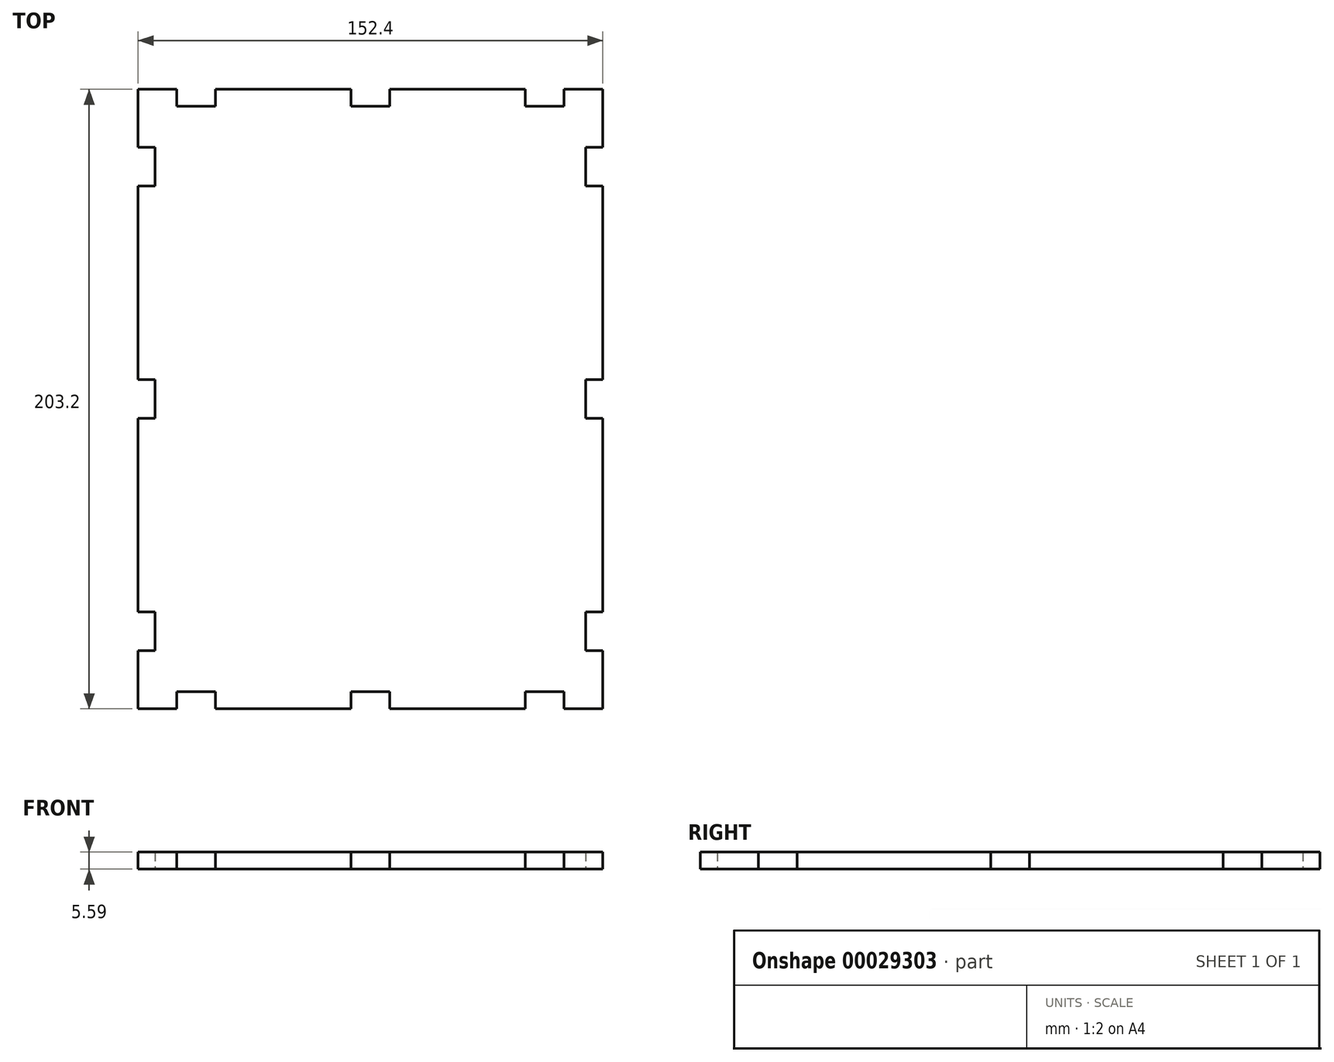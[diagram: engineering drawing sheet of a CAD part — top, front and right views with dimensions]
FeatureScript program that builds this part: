
annotation { "Feature Type Name" : "Feature", "Feature Type Description" : "" }
export const myFeature = defineFeature(function(context is Context, id is Id, definition is map)
    precondition{}
    {
        {
            var Q0;
            Q0=qCreatedBy(makeId("Top.planeOp"),FACE);
            var sketch = newSketch(context, id + "F0", { "sketchPlane" : qUnion([Q0])});
            skLineSegment(sketch, "E0", {"start": v(0, -101.6) * mm, "end": v(0, 101.6) * mm, "construction": true});
            skLineSegment(sketch, "E1", {"start": v(-76.2, 0) * mm, "end": v(76.2, 0) * mm, "construction": true});
            skLineSegment(sketch, "E2.0", {"start": v(38.1, -101.6) * mm, "end": v(38.1, 101.6) * mm, "construction": true});
            skLineSegment(sketch, "E3.0", {"start": v(76.2, -101.6) * mm, "end": v(76.2, -82.55) * mm, "construction": true});
            skLineSegment(sketch, "E4.0", {"start": v(-38.1, -101.6) * mm, "end": v(-38.1, 101.6) * mm, "construction": true});
            skLineSegment(sketch, "E5.0", {"start": v(-76.2, -101.6) * mm, "end": v(-76.2, 76.2) * mm, "construction": true});
            skLineSegment(sketch, "E6.0", {"start": v(-76.2, -50.8) * mm, "end": v(76.2, -50.8) * mm, "construction": true});
            skLineSegment(sketch, "E7.0", {"start": v(-76.2, -101.6) * mm, "end": v(-63.5, -101.6) * mm, "construction": true});
            skLineSegment(sketch, "E8.0", {"start": v(-76.2, 50.8) * mm, "end": v(76.2, 50.8) * mm, "construction": true});
            skLineSegment(sketch, "E9.0", {"start": v(-76.2, 101.6) * mm, "end": v(76.2, 101.6) * mm, "construction": true});
            skLineSegment(sketch, "E10.bottom", {"start": v(-76.2, -101.6) * mm, "end": v(-63.5, -101.6) * mm});
            skLineSegment(sketch, "E10.top", {"start": v(-76.2, 101.6) * mm, "end": v(-63.5, 101.6) * mm});
            skLineSegment(sketch, "E10.left", {"start": v(-76.2, -101.6) * mm, "end": v(-76.2, -82.55) * mm});
            skLineSegment(sketch, "E10.right", {"start": v(76.2, -101.6) * mm, "end": v(76.2, -82.55) * mm});
            skLineSegment(sketch, "E11.0", {"start": v(-57.15, -101.6) * mm, "end": v(-57.15, 101.6) * mm, "construction": true});
            skLineSegment(sketch, "E12.0", {"start": v(57.15, -101.6) * mm, "end": v(57.15, 101.6) * mm, "construction": true});
            skLineSegment(sketch, "E13.0", {"start": v(-76.2, -76.2) * mm, "end": v(76.2, -76.2) * mm, "construction": true});
            skLineSegment(sketch, "E14.0", {"start": v(-76.2, 76.2) * mm, "end": v(76.2, 76.2) * mm, "construction": true});
            skLineSegment(sketch, "E15.0", {"start": v(-76.2, -69.85) * mm, "end": v(76.2, -69.85) * mm, "construction": true});
            skLineSegment(sketch, "E16.0", {"start": v(-76.2, -82.55) * mm, "end": v(76.2, -82.55) * mm, "construction": true});
            skLineSegment(sketch, "E17.0", {"start": v(-70.61, -101.6) * mm, "end": v(-70.61, 101.6) * mm, "construction": true});
            skLineSegment(sketch, "E18.0", {"start": v(-76.2, -96.01) * mm, "end": v(76.2, -96.01) * mm, "construction": true});
            skLineSegment(sketch, "E19.0", {"start": v(-76.2, 96.01) * mm, "end": v(76.2, 96.01) * mm, "construction": true});
            skLineSegment(sketch, "E20.0", {"start": v(70.61, -101.6) * mm, "end": v(70.61, 101.6) * mm, "construction": true});
            skLineSegment(sketch, "E21", {"start": v(-76.2, -82.55) * mm, "end": v(-70.61, -82.55) * mm});
            skLineSegment(sketch, "E22", {"start": v(-70.61, -82.55) * mm, "end": v(-70.61, -69.85) * mm});
            skLineSegment(sketch, "E23", {"start": v(-70.61, -69.85) * mm, "end": v(-76.2, -69.85) * mm});
            skLineSegment(sketch, "E24", {"start": v(76.2, -82.55) * mm, "end": v(70.61, -82.55) * mm});
            skLineSegment(sketch, "E25", {"start": v(70.61, -82.55) * mm, "end": v(70.61, -69.85) * mm});
            skLineSegment(sketch, "E26", {"start": v(70.61, -69.85) * mm, "end": v(76.2, -69.85) * mm});
            skLineSegment(sketch, "E27.0", {"start": v(-76.2, 6.35) * mm, "end": v(76.2, 6.35) * mm, "construction": true});
            skLineSegment(sketch, "E28.0", {"start": v(-76.2, -6.35) * mm, "end": v(76.2, -6.35) * mm, "construction": true});
            skLineSegment(sketch, "E29", {"start": v(-76.2, -6.35) * mm, "end": v(-70.61, -6.35) * mm});
            skLineSegment(sketch, "E30.0", {"start": v(-76.2, 82.55) * mm, "end": v(76.2, 82.55) * mm, "construction": true});
            skLineSegment(sketch, "E31.0", {"start": v(-76.2, 69.85) * mm, "end": v(76.2, 69.85) * mm, "construction": true});
            skLineSegment(sketch, "E32", {"start": v(-70.61, -6.35) * mm, "end": v(-70.61, 6.35) * mm});
            skLineSegment(sketch, "E33", {"start": v(-70.61, 6.35) * mm, "end": v(-76.2, 6.35) * mm});
            skLineSegment(sketch, "E34", {"start": v(-76.2, 69.85) * mm, "end": v(-70.61, 69.85) * mm});
            skLineSegment(sketch, "E35", {"start": v(-70.61, 69.85) * mm, "end": v(-70.61, 82.55) * mm});
            skLineSegment(sketch, "E36", {"start": v(-70.61, 82.55) * mm, "end": v(-76.2, 82.55) * mm});
            skLineSegment(sketch, "E37", {"start": v(76.2, 69.85) * mm, "end": v(70.61, 69.85) * mm});
            skLineSegment(sketch, "E38", {"start": v(70.61, 69.85) * mm, "end": v(70.61, 82.55) * mm});
            skLineSegment(sketch, "E39", {"start": v(70.61, 82.55) * mm, "end": v(76.2, 82.55) * mm});
            skLineSegment(sketch, "E40", {"start": v(76.2, 6.35) * mm, "end": v(70.61, 6.35) * mm});
            skLineSegment(sketch, "E41", {"start": v(70.61, 6.35) * mm, "end": v(70.61, -6.35) * mm});
            skLineSegment(sketch, "E42", {"start": v(70.61, -6.35) * mm, "end": v(76.2, -6.35) * mm});
            skLineSegment(sketch, "E43.0", {"start": v(-63.5, -101.6) * mm, "end": v(-63.5, 101.6) * mm, "construction": true});
            skLineSegment(sketch, "E44.0", {"start": v(-50.8, -101.6) * mm, "end": v(-50.8, 101.6) * mm, "construction": true});
            skLineSegment(sketch, "E45.0", {"start": v(-6.35, -101.6) * mm, "end": v(-6.35, 101.6) * mm, "construction": true});
            skLineSegment(sketch, "E46.0", {"start": v(6.35, -101.6) * mm, "end": v(6.35, 101.6) * mm, "construction": true});
            skLineSegment(sketch, "E47.0", {"start": v(50.8, -101.6) * mm, "end": v(50.8, 101.6) * mm, "construction": true});
            skLineSegment(sketch, "E48.0", {"start": v(63.5, -101.6) * mm, "end": v(63.5, 101.6) * mm, "construction": true});
            skLineSegment(sketch, "E49", {"start": v(-63.5, -101.6) * mm, "end": v(-63.5, -96.01) * mm});
            skLineSegment(sketch, "E50", {"start": v(-63.5, -96.01) * mm, "end": v(-50.8, -96.01) * mm});
            skLineSegment(sketch, "E51", {"start": v(-50.8, -96.01) * mm, "end": v(-50.8, -101.6) * mm});
            skLineSegment(sketch, "E52", {"start": v(-6.35, -101.6) * mm, "end": v(-6.35, -96.01) * mm});
            skLineSegment(sketch, "E53", {"start": v(-6.35, -96.01) * mm, "end": v(6.35, -96.01) * mm});
            skLineSegment(sketch, "E54", {"start": v(6.35, -96.01) * mm, "end": v(6.35, -101.6) * mm});
            skLineSegment(sketch, "E55", {"start": v(50.8, -101.6) * mm, "end": v(50.8, -96.01) * mm});
            skLineSegment(sketch, "E56", {"start": v(50.8, -96.01) * mm, "end": v(63.5, -96.01) * mm});
            skLineSegment(sketch, "E57", {"start": v(63.5, -96.01) * mm, "end": v(63.5, -101.6) * mm});
            skLineSegment(sketch, "E58.trimOffspring", {"start": v(63.5, -101.6) * mm, "end": v(76.2, -101.6) * mm});
            skLineSegment(sketch, "E59.trimOffspring", {"start": v(76.2, -69.85) * mm, "end": v(76.2, -6.35) * mm});
            skLineSegment(sketch, "E60.trimOffspring", {"start": v(76.2, -69.85) * mm, "end": v(76.2, -6.35) * mm, "construction": true});
            skLineSegment(sketch, "E61.trimOffspring", {"start": v(76.2, 6.35) * mm, "end": v(76.2, 69.85) * mm});
            skLineSegment(sketch, "E62.trimOffspring", {"start": v(76.2, 6.35) * mm, "end": v(76.2, 69.85) * mm, "construction": true});
            skLineSegment(sketch, "E63.trimOffspring", {"start": v(76.2, 82.55) * mm, "end": v(76.2, 101.6) * mm});
            skLineSegment(sketch, "E64.trimOffspring", {"start": v(76.2, 82.55) * mm, "end": v(76.2, 101.6) * mm, "construction": true});
            skLineSegment(sketch, "E65.trimOffspring", {"start": v(-76.2, 82.55) * mm, "end": v(-76.2, 101.6) * mm});
            skLineSegment(sketch, "E66.trimOffspring", {"start": v(-76.2, 82.55) * mm, "end": v(-76.2, 101.6) * mm, "construction": true});
            skLineSegment(sketch, "E67.trimOffspring", {"start": v(-76.2, 6.35) * mm, "end": v(-76.2, 69.85) * mm});
            skLineSegment(sketch, "E68.trimOffspring", {"start": v(-76.2, -69.85) * mm, "end": v(-76.2, -6.35) * mm});
            skLineSegment(sketch, "E69.trimOffspring", {"start": v(-50.8, -101.6) * mm, "end": v(-6.35, -101.6) * mm});
            skLineSegment(sketch, "E70.trimOffspring", {"start": v(-57.15, -101.6) * mm, "end": v(76.2, -101.6) * mm, "construction": true});
            skLineSegment(sketch, "E71.trimOffspring", {"start": v(6.35, -101.6) * mm, "end": v(50.8, -101.6) * mm});
            skLineSegment(sketch, "E72", {"start": v(-63.5, 101.6) * mm, "end": v(-63.5, 96.01) * mm});
            skLineSegment(sketch, "E73", {"start": v(-63.5, 96.01) * mm, "end": v(-50.8, 96.01) * mm});
            skLineSegment(sketch, "E74", {"start": v(-50.8, 96.01) * mm, "end": v(-50.8, 101.6) * mm});
            skLineSegment(sketch, "E75", {"start": v(-6.35, 101.6) * mm, "end": v(-6.35, 96.01) * mm});
            skLineSegment(sketch, "E76", {"start": v(-6.35, 96.01) * mm, "end": v(6.35, 96.01) * mm});
            skLineSegment(sketch, "E77", {"start": v(6.35, 96.01) * mm, "end": v(6.35, 101.6) * mm});
            skLineSegment(sketch, "E78", {"start": v(50.8, 101.6) * mm, "end": v(50.8, 96.01) * mm});
            skLineSegment(sketch, "E79", {"start": v(50.8, 96.01) * mm, "end": v(63.5, 96.01) * mm});
            skLineSegment(sketch, "E80", {"start": v(63.5, 96.01) * mm, "end": v(63.5, 101.6) * mm});
            skLineSegment(sketch, "E81.trimOffspring", {"start": v(63.5, 101.6) * mm, "end": v(76.2, 101.6) * mm});
            skLineSegment(sketch, "E82.trimOffspring", {"start": v(6.35, 101.6) * mm, "end": v(50.8, 101.6) * mm});
            skLineSegment(sketch, "E83.trimOffspring", {"start": v(-50.8, 101.6) * mm, "end": v(-6.35, 101.6) * mm});
            skSolve(sketch);
        }
        {
            var Q0;
            Q0=makeQuery(id+"F0.imprint","IMPRINT",FACE,{"disambiguationData":[TD([[makeQuery(id+"F0.imprint","IMPRINT",EDGE,{"derivedFrom":sQuery(id+"F0.wireOp",EDGE,"E10.bottom")}),1.0]])]});
            extrude(context, id + "F1", {"entities" : qUnion([Q0]), "depth" : 5.6 * mm});
        }
    });
